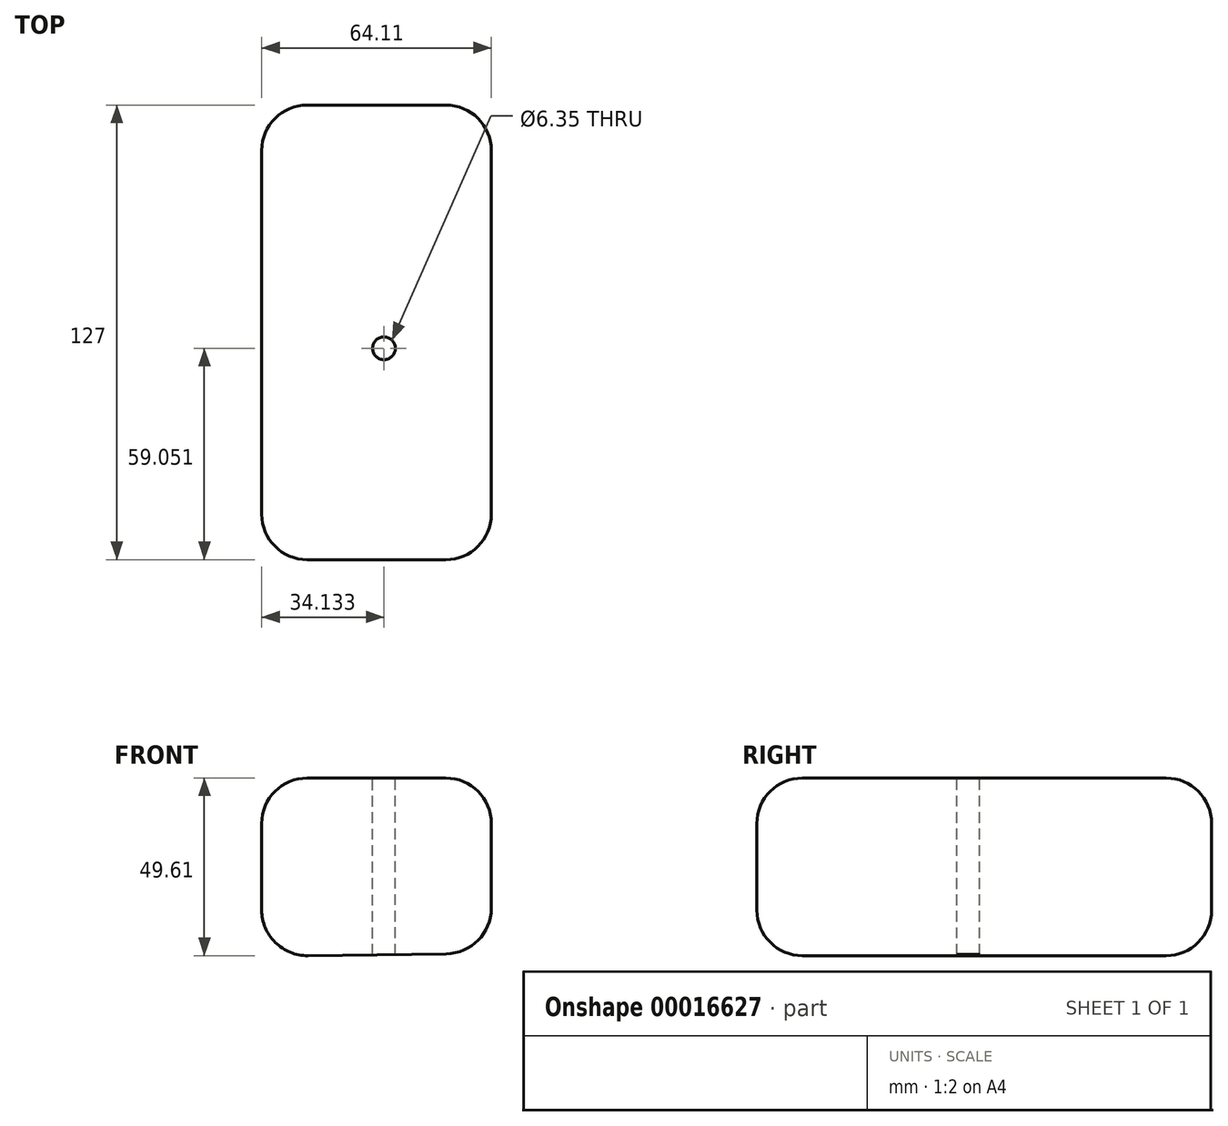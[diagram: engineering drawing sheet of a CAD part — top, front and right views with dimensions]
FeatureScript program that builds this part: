
annotation { "Feature Type Name" : "Feature", "Feature Type Description" : "" }
export const myFeature = defineFeature(function(context is Context, id is Id, definition is map)
    precondition{}
    {
        {
            var Q0;
            Q0=qCreatedBy(makeId("Front.planeOp"),FACE);
            var sketch = newSketch(context, id + "F0", { "sketchPlane" : qUnion([Q0])});
            skLineSegment(sketch, "E0", {"start": v(-115.92, 10.05) * mm, "end": v(-115.92, 59.82) * mm});
            skLineSegment(sketch, "E1", {"start": v(-115.92, 59.82) * mm, "end": v(-51.81, 59.82) * mm});
            skLineSegment(sketch, "E2", {"start": v(-51.81, 59.82) * mm, "end": v(-51.81, 10.86) * mm});
            skLineSegment(sketch, "E3", {"start": v(-51.81, 10.86) * mm, "end": v(-115.92, 10.05) * mm});
            skSolve(sketch);
        }
        {
            var Q0;
            Q0=makeQuery(id+"F0.imprint","IMPRINT",FACE,{"disambiguationData":[TD([[makeQuery(id+"F0.imprint","IMPRINT",EDGE,{"derivedFrom":sQuery(id+"F0.wireOp",EDGE,"E0")}),-1.0]])]});
            extrude(context, id + "F1", {"entities" : qUnion([Q0]), "depth" : 127 * mm});
        }
        {
            var Q0;
            Q0=makeQuery(id+"F1.opExtrude","CAP_EDGE",EDGE,{"disambiguationData":[OSD([sQuery(id+"F0.wireOp",EDGE,"E1")])],"isStart":false});
            var Q1;
            Q1=makeQuery(id+"F1.opExtrude","SWEPT_EDGE",EDGE,{"disambiguationData":[OSD([sQuery(id+"F0.wireOp",EDGE,"E0"),sQuery(id+"F0.wireOp",EDGE,"E1")])]});
            var Q2;
            Q2=makeQuery(id+"F1.opExtrude","CAP_EDGE",EDGE,{"disambiguationData":[OSD([sQuery(id+"F0.wireOp",EDGE,"E1")])],"isStart":true});
            var Q3;
            Q3=makeQuery(id+"F1.opExtrude","SWEPT_EDGE",EDGE,{"disambiguationData":[OSD([sQuery(id+"F0.wireOp",EDGE,"E1"),sQuery(id+"F0.wireOp",EDGE,"E2")])]});
            var Q4;
            Q4=makeQuery(id+"F1.opExtrude","CAP_EDGE",EDGE,{"disambiguationData":[OSD([sQuery(id+"F0.wireOp",EDGE,"E2")])],"isStart":false});
            var Q5;
            Q5=makeQuery(id+"F1.opExtrude","CAP_FACE",FACE,{"disambiguationData":[OSD([sQuery(id+"F0.wireOp",EDGE,"E0"),sQuery(id+"F0.wireOp",EDGE,"E1"),sQuery(id+"F0.wireOp",EDGE,"E2"),sQuery(id+"F0.wireOp",EDGE,"E3")])],"isStart":false});
            var Q6;
            Q6=makeQuery(id+"F1.opExtrude","CAP_EDGE",EDGE,{"disambiguationData":[OSD([sQuery(id+"F0.wireOp",EDGE,"E2")])],"isStart":true});
            var Q7;
            Q7=makeQuery(id+"F1.opExtrude","SWEPT_EDGE",EDGE,{"disambiguationData":[OSD([sQuery(id+"F0.wireOp",EDGE,"E2"),sQuery(id+"F0.wireOp",EDGE,"E3")])]});
            var Q8;
            Q8=makeQuery(id+"F1.opExtrude","CAP_EDGE",EDGE,{"disambiguationData":[OSD([sQuery(id+"F0.wireOp",EDGE,"E3")])],"isStart":false});
            var Q9;
            Q9=makeQuery(id+"F1.opExtrude","CAP_EDGE",EDGE,{"disambiguationData":[OSD([sQuery(id+"F0.wireOp",EDGE,"E0")])],"isStart":false});
            var Q10;
            Q10=makeQuery(id+"F1.opExtrude","CAP_EDGE",EDGE,{"disambiguationData":[OSD([sQuery(id+"F0.wireOp",EDGE,"E0")])],"isStart":true});
            var Q11;
            Q11=makeQuery(id+"F1.opExtrude","SWEPT_EDGE",EDGE,{"disambiguationData":[OSD([sQuery(id+"F0.wireOp",EDGE,"E0"),sQuery(id+"F0.wireOp",EDGE,"E3")])]});
            var Q12;
            Q12=makeQuery(id+"F1.opExtrude","CAP_EDGE",EDGE,{"disambiguationData":[OSD([sQuery(id+"F0.wireOp",EDGE,"E3")])],"isStart":true});
            fillet(context, id + "F2", {"entities" : qUnion([Q0, Q1, Q2, Q3, Q4, Q5, Q6, Q7, Q8, Q9, Q10, Q11, Q12]), "radius" : 12.7 * mm, "tangentPropagation" : true, "allowEdgeOverflow" : false});
        }
        {
            var Q0;
            Q0=makeQuery(id+"F1.opExtrude","SWEPT_FACE",FACE,{"disambiguationData":[OSD([sQuery(id+"F0.wireOp",EDGE,"E1")])]});
            var sketch = newSketch(context, id + "F3", { "sketchPlane" : qUnion([Q0])});
            skCircle(sketch, "E4", {"center": v(-81.79, -67.95) * mm, "radius": 8.1 * mm});
            skSolve(sketch);
        }
        {
            var Q0;
            Q0=sQuery(id+"F3.wireOp",VERTEX,"E4.center");
            var Q1;
            Q1=makeQuery(id+"F1.opExtrude","SWEPT_BODY",BODY,{"disambiguationData":[OSD([sQuery(id+"F0.wireOp",EDGE,"E0"),sQuery(id+"F0.wireOp",EDGE,"E1"),sQuery(id+"F0.wireOp",EDGE,"E2"),sQuery(id+"F0.wireOp",EDGE,"E3")])]});
            hole(context, id + "F4", {"style" : HoleStyle.SIMPLE, "holeDiameter" : 6.35 * mm, "endStyle" : HoleEndStyle.THROUGH, "locations" : qUnion([Q0]), "scope" : qUnion([Q1])});
        }
    });
